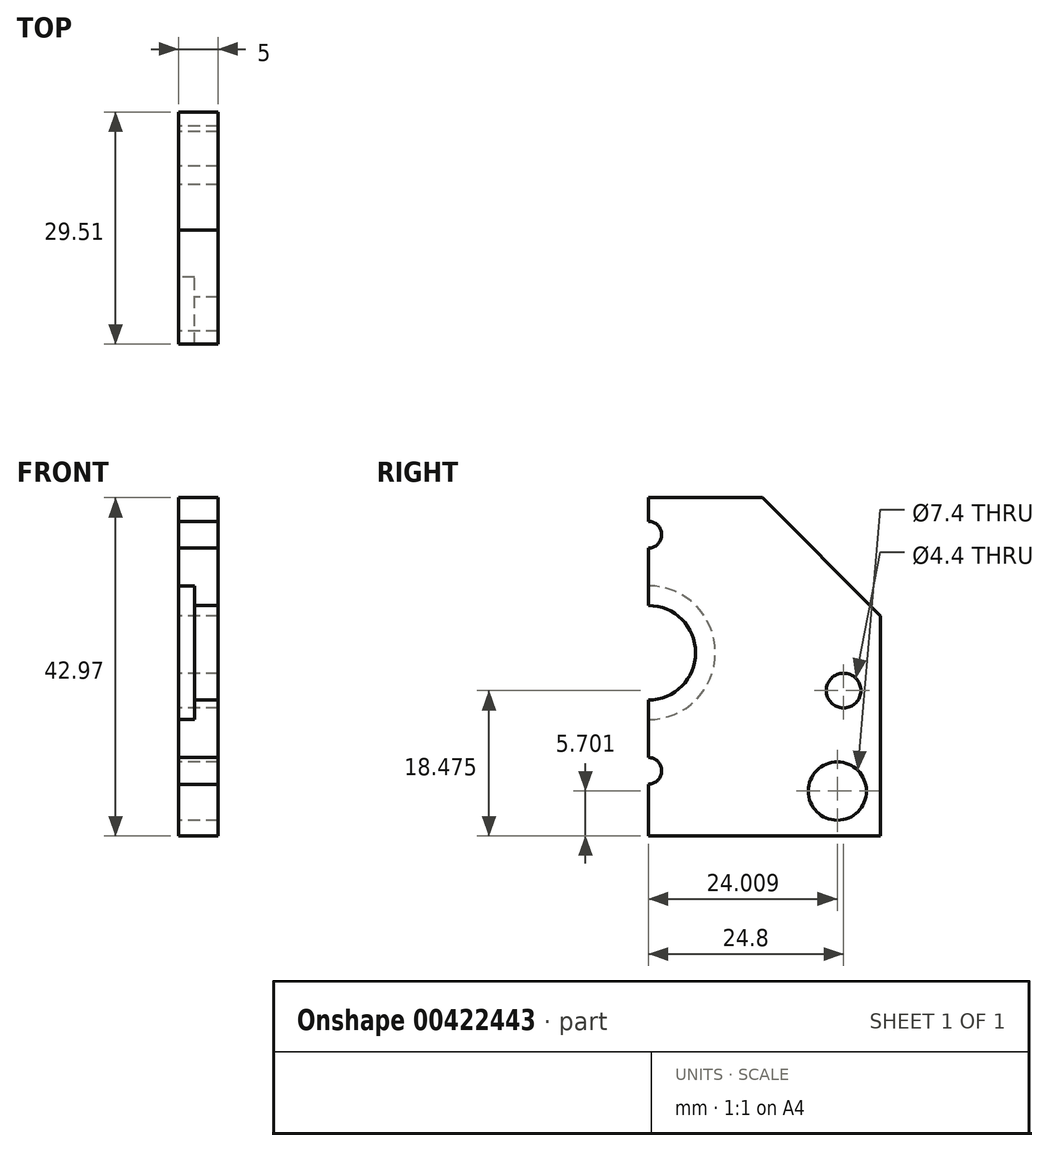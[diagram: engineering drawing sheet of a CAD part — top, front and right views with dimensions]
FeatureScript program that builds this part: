
annotation { "Feature Type Name" : "Feature", "Feature Type Description" : "" }
export const myFeature = defineFeature(function(context is Context, id is Id, definition is map)
    precondition{}
    {
        {
            var Q0;
            Q0=qCreatedBy(makeId("Right.planeOp"),FACE);
            var sketch = newSketch(context, id + "F0", { "sketchPlane" : qUnion([Q0])});
            skLineSegment(sketch, "E0.top", {"start": v(-33.37, 5.37) * mm, "end": v(-3.86, 5.37) * mm});
            skLineSegment(sketch, "E0.right", {"start": v(-3.86, 33.34) * mm, "end": v(-3.86, 5.37) * mm});
            skLineSegment(sketch, "E1", {"start": v(-33.37, 48.34) * mm, "end": v(-18.86, 48.34) * mm});
            skArc(sketch, "E2", {"start": v(-33.37, 22.64) * mm, "mid": v(-27.37, 28.64) * mm, "end": v(-33.37, 34.64) * mm});
            skCircle(sketch, "E3", {"center": v(-9.36, 11.07) * mm, "radius": 3.7 * mm});
            skCircle(sketch, "E4", {"center": v(-8.57, 23.84) * mm, "radius": 2.2 * mm});
            skPoint(sketch, "E4.first.point", {"position": v(-7.89, 25.94) * mm});
            skPoint(sketch, "E4.second.point", {"position": v(-10.75, 24.15) * mm});
            skPoint(sketch, "E4.third.point", {"position": v(-6.74, 22.62) * mm});
            skArc(sketch, "E5", {"start": v(-33.37, 41.94) * mm, "mid": v(-31.67, 43.64) * mm, "end": v(-33.37, 45.34) * mm});
            skPoint(sketch, "E5.second.point", {"position": v(-31.8, 43) * mm});
            skArc(sketch, "E6", {"start": v(-33.37, 11.94) * mm, "mid": v(-31.67, 13.64) * mm, "end": v(-33.37, 15.34) * mm});
            skPoint(sketch, "E6.third.point", {"position": v(-32.23, 12.39) * mm});
            skLineSegment(sketch, "E7", {"start": v(-18.86, 48.34) * mm, "end": v(-3.86, 33.34) * mm});
            skLineSegment(sketch, "E8", {"start": v(-33.37, 48.34) * mm, "end": v(-33.37, 5.37) * mm});
            skArc(sketch, "E9", {"start": v(-33.37, 20.14) * mm, "mid": v(-24.87, 28.64) * mm, "end": v(-33.37, 37.14) * mm});
            skSolve(sketch);
        }
        {
            var Q0;
            Q0=makeQuery(id+"F0.imprint","IMPRINT",FACE,{"disambiguationData":[TD([[makeQuery(id+"F0.imprint","IMPRINT",EDGE,{"derivedFrom":sQuery(id+"F0.wireOp",EDGE,"E0.top")}),1.0]])]});
            extrude(context, id + "F1", {"entities" : qUnion([Q0]), "depth" : 5 * mm});
        }
        {
            var Q0;
            Q0=qSketchRegion(id+"F0",true);
            var Q1;
            Q1=makeQuery(id+"F0.imprint","IMPRINT",FACE,{"disambiguationData":[TD([[makeQuery(id+"F0.imprint","IMPRINT",EDGE,{"derivedFrom":sQuery(id+"F0.wireOp",EDGE,"54432049-e9b1-4224-a011-6ff6c7ef2d78")}),1.0]])]});
            extrude(context, id + "F2", {"entities" : qUnion([Q0, Q1]), "operationType" : NewBodyOperationType.ADD, "depth" : 3 * mm});
        }
        {
            var Q0;
            {var subQ0=sQuery(id+"F0.wireOp",EDGE,"E2");Q0=makeQuery(id+"F0.imprint","IMPRINT",FACE,{"disambiguationData":[TD([[makeQuery(id+"F0.imprint","IMPRINT",EDGE,{"derivedFrom":subQ0}),1.0]])]});}
            var Q1;
            {var subQ0=sQuery(id+"F0.wireOp",EDGE,"E5");Q1=makeQuery(id+"F0.imprint","IMPRINT",FACE,{"disambiguationData":[TD([[makeQuery(id+"F0.imprint","IMPRINT",EDGE,{"derivedFrom":subQ0}),1.0]])]});}
            var Q2;
            {var subQ0=sQuery(id+"F0.wireOp",EDGE,"E6");Q2=makeQuery(id+"F0.imprint","IMPRINT",FACE,{"disambiguationData":[TD([[makeQuery(id+"F0.imprint","IMPRINT",EDGE,{"derivedFrom":subQ0}),1.0]])]});}
            extrude(context, id + "F3", {"entities" : qUnion([Q0, Q1, Q2]), "operationType" : NewBodyOperationType.REMOVE, "endBound" : BoundingType.THROUGH_ALL, "depth" : 25 * mm});
        }
        {
            var Q0;
            {var subQ0=sQuery(id+"F0.wireOp",EDGE,"E8");var subQ1=sQuery(id+"F0.wireOp",EDGE,"E0.top");var subQ3=sQuery(id+"F0.wireOp",EDGE,"E9");var subQ5=sQuery(id+"F0.wireOp",EDGE,"E1");Q0=makeQuery(id+"F2.boolean.opBoolean","SPLIT",FACE,{"disambiguationData":[TD([makeQuery(id+"F1.opExtrude","SWEPT_FACE",FACE,{"disambiguationData":[OSD([subQ3])]})])],"derivedFrom":makeQuery(id+"F2.opExtrude","CAP_FACE",FACE,{"disambiguationData":[OSD([subQ1,sQuery(id+"F0.wireOp",EDGE,"E0.right"),subQ5,sQuery(id+"F0.wireOp",EDGE,"E3"),sQuery(id+"F0.wireOp",EDGE,"E4"),sQuery(id+"F0.wireOp",EDGE,"E7"),subQ0])],"isStart":false})});}
            var Q1;
            Q1=makeQuery(id+"F1.opExtrude","CAP_FACE",FACE,{"disambiguationData":[OSD([sQuery(id+"F0.wireOp",EDGE,"E0.top"),sQuery(id+"F0.wireOp",EDGE,"E0.right"),sQuery(id+"F0.wireOp",EDGE,"E1"),sQuery(id+"F0.wireOp",EDGE,"E3"),sQuery(id+"F0.wireOp",EDGE,"E4"),sQuery(id+"F0.wireOp",EDGE,"E5"),sQuery(id+"F0.wireOp",EDGE,"E6"),sQuery(id+"F0.wireOp",EDGE,"E7"),sQuery(id+"F0.wireOp",EDGE,"E8"),sQuery(id+"F0.wireOp",EDGE,"E9")])],"isStart":false});
            extrude(context, id + "F4", {"entities" : qUnion([Q0]), "operationType" : NewBodyOperationType.ADD, "endBound" : BoundingType.UP_TO_SURFACE, "endBoundEntityFace" : qUnion([Q1]), "depth" : 25 * mm});
        }
        {
            var Q0;
            {var subQ0=sQuery(id+"F0.wireOp",EDGE,"E2");Q0=makeQuery(id+"F0.imprint","IMPRINT",FACE,{"disambiguationData":[TD([[makeQuery(id+"F0.imprint","IMPRINT",EDGE,{"derivedFrom":subQ0}),-1.0]])]});}
            extrude(context, id + "F5", {"entities" : qUnion([Q0]), "operationType" : NewBodyOperationType.REMOVE, "depth" : 2 * mm});
        }
    });
